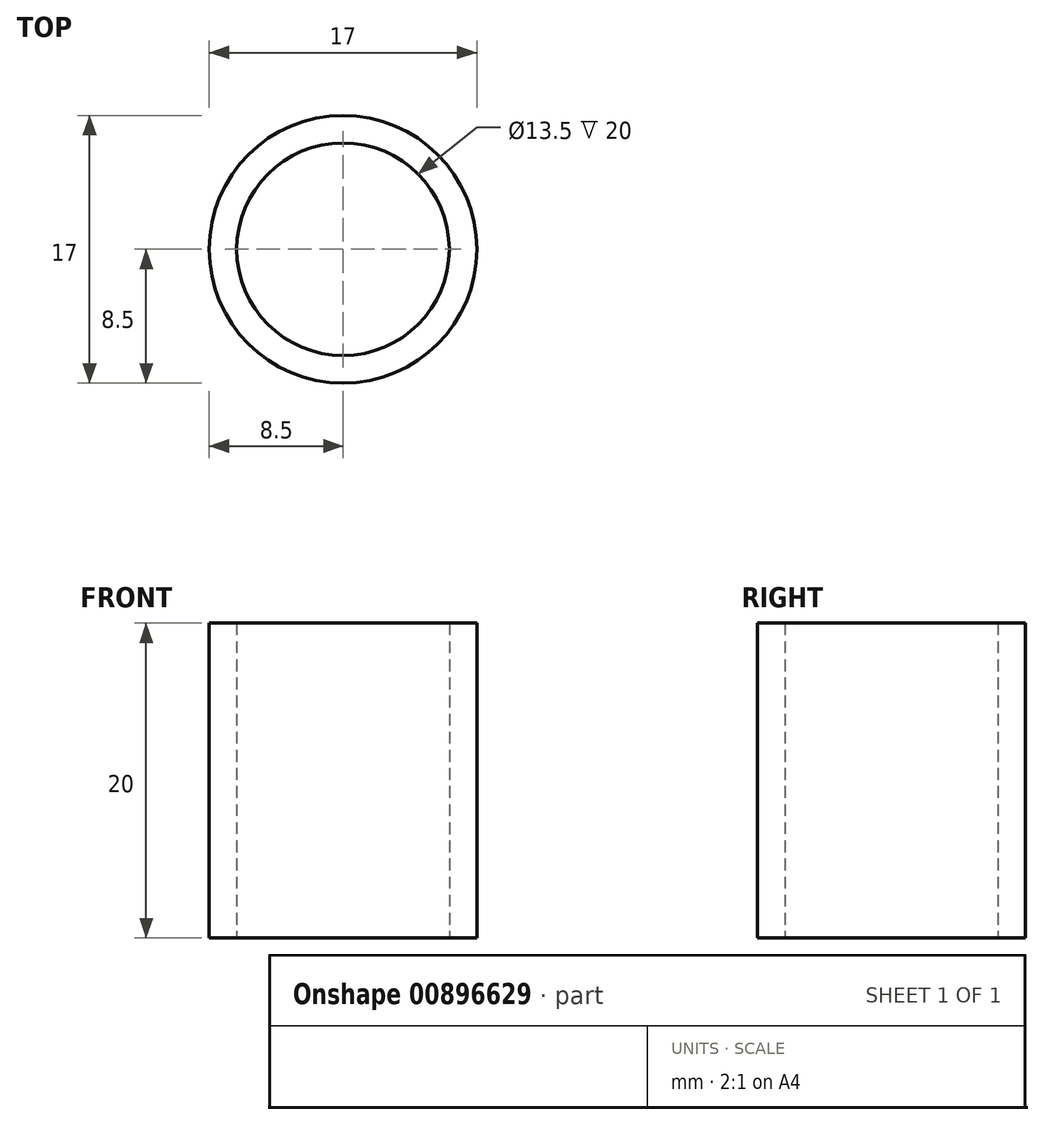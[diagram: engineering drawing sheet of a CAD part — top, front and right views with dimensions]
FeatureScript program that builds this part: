
annotation { "Feature Type Name" : "Feature", "Feature Type Description" : "" }
export const myFeature = defineFeature(function(context is Context, id is Id, definition is map)
    precondition{}
    {
        {
            var Q0;
            Q0=qCreatedBy(makeId("Top.planeOp"),FACE);
            var sketch = newSketch(context, id + "F0", { "sketchPlane" : qUnion([Q0])});
            skCircle(sketch, "E0", {"center": v(0, 0) * mm, "radius": 6.75 * mm});
            skCircle(sketch, "E1", {"center": v(0, 0) * mm, "radius": 8.5 * mm});
            skSolve(sketch);
        }
        {
            var Q0;
            Q0 = qSketchRegion(id + "F0", true);
            extrude(context, id + "F1", {"entities" : qUnion([Q0]), "depth" : 20 * mm, "offsetDistance" : 25 * mm});
        }
    });
